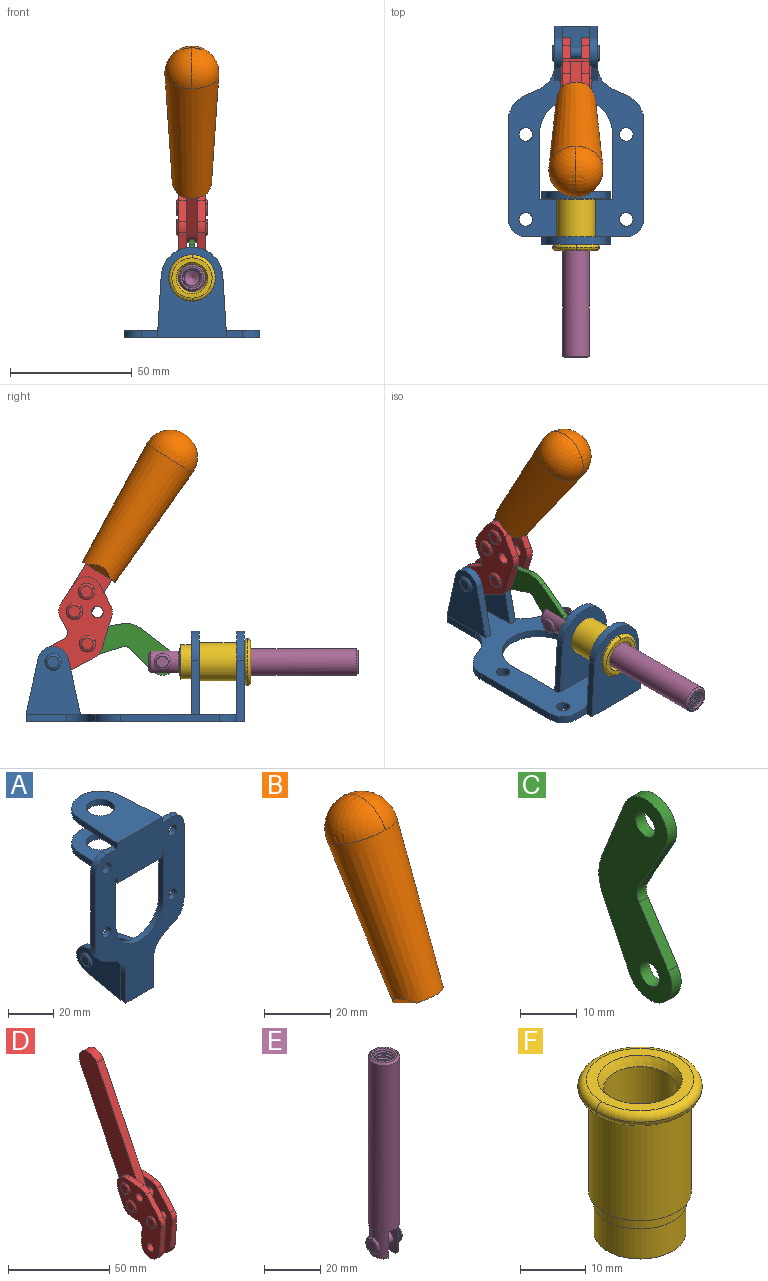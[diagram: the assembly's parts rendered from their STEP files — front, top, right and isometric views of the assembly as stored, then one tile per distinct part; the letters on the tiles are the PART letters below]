
ASSEMBLY  parts=6 mates=6
PART A: 55 faces, bbox 55.7x37.4x89.8 mm
  f0: torus R=2.41mm, axis (-1,0,0), area 15mm2, adj f11,f15,f25
  f1: torus R=2.41mm, axis (-1,0,0), area 15mm2, adj f10,f12,f22
  f2: cylinder r=2.78mm len=5.56mm, axis (0,-1,0), area 54.2mm2, adj f30,f54
  f3: cylinder r=14.99mm len=29.97mm, axis (0,-1,0), area 145.9mm2, adj f30,f49,f53,f54
  f4: cylinder r=2.78mm len=5.56mm, axis (0,-1,0), area 54.2mm2, adj f30,f54
  f5: cylinder r=2.78mm len=5.56mm, axis (0,-1,0), area 54.2mm2, adj f30,f54
  f6: cylinder r=2.78mm len=5.56mm, axis (0,-1,0), area 54.2mm2, adj f30,f54
  f7: cylinder r=6.35mm len=12.7mm, axis (0,0,1), area 123.6mm2, adj f27,f51
  f8: cylinder r=6.35mm len=12.7mm, axis (0,0,-1), area 124.7mm2, adj f21,f35
  f9: cylinder r=2.41mm len=11.18mm, axis (-1,0,0), area 169.4mm2, adj f16,f19
  f10: plane 4.83x4.83mm, normal (1,0,0), area 18.3mm2, adj f1,f12
  f11: plane 4.83x4.83mm, normal (-1,0,0), area 18.3mm2, adj f0,f15
  f12: torus R=2.41mm, axis (-1,0,0), area 15mm2, adj f1,f10,f22
  f13: cylinder r=6.35mm len=12.41mm, axis (1,0,0), area 53.4mm2, adj f18,f19,f22,f23
  f14: cylinder r=6.35mm len=12.41mm, axis (-1,0,0), area 53.4mm2, adj f16,f17,f24,f25
  f15: torus R=2.41mm, axis (-1,0,0), area 15mm2, adj f0,f11,f25
  f16: plane 27.86x22.35mm, normal (1,0,0), area 425.4mm2, adj f9,f14,f17,f24,f30
  f17: plane 22.86x4.97mm, normal (0,0.21,0.98), area 72.5mm2, adj f14,f16,f25,f30
  f18: plane 22.86x4.97mm, normal (0,0.21,0.98), area 72.5mm2, adj f13,f19,f22,f30
  f19: plane 27.86x22.35mm, normal (-1,0,0), area 425.4mm2, adj f9,f13,f18,f23,f30
  f20: cylinder r=12.7mm len=25.35mm, axis (0,0,-1), area 119.8mm2, adj f21,f34,f35,f36
  f21: plane 34.21x28.07mm, normal (0,0,-1), area 702.4mm2, adj f8,f20,f30,f34,f36
  f22: plane 27.96x22.45mm, normal (1,0,0), area 407.2mm2, adj f1,f12,f13,f18,f23,f30,f42,f43
  f23: plane 22.86x4.97mm, normal (0,0.21,-0.98), area 72.5mm2, adj f13,f19,f22,f44
  f24: plane 22.86x4.97mm, normal (0,0.21,-0.98), area 72.5mm2, adj f14,f16,f25,f44
  f25: plane 27.86x22.35mm, normal (-1,0,0), area 407.1mm2, adj f0,f14,f15,f17,f24,f30,f45,f46
  f26: plane 3.1x0.95mm, normal (0,0,-1), area 2.7mm2, adj f30,f49,f50,f54
  f27: plane 34.21x28.07mm, normal (0,0,1), area 702.4mm2, adj f7,f28,f30,f50,f52
  f28: cylinder r=12.7mm len=25.35mm, axis (0,0,1), area 118.8mm2, adj f27,f50,f51,f52
  f29: plane 3.1x0.95mm, normal (0,0,-1), area 2.7mm2, adj f30,f52,f53,f54
  f30: plane 86.54x55.63mm, normal (0,1,0), area 2362.9mm2, adj f2,f3,f4,f5,f6,f16,f17,f18
  f31: plane 40.56x3.1mm, normal (-1,0,0), area 125.7mm2, adj f30,f32,f48,f54
  f32: cylinder r=7.11mm len=7.11mm, axis (0,-1,0), area 34.6mm2, adj f30,f31,f33,f54
  f33: plane 6.67x3.1mm, normal (0,0,1), area 20.4mm2, adj f30,f32,f34,f54
  f34: plane 25.39x3.13mm, normal (-1,0.06,0), area 79.5mm2, adj f20,f21,f33,f35,f54
  f35: plane 37.31x28.45mm, normal (0,0,1), area 789.9mm2, adj f8,f20,f34,f36,f54
  f36: plane 25.39x3.13mm, normal (1,0.06,0), area 79.5mm2, adj f20,f21,f35,f37,f54
  f37: plane 6.67x3.1mm, normal (0,0,1), area 20.4mm2, adj f30,f36,f38,f54
  f38: cylinder r=7.11mm len=7.11mm, axis (0,-1,0), area 34.6mm2, adj f30,f37,f39,f54
  f39: plane 40.56x3.1mm, normal (1,0,0), area 125.7mm2, adj f30,f38,f40,f54
  f40: cylinder r=11.18mm len=10.16mm, axis (0,-1,0), area 39.5mm2, adj f30,f39,f41,f54
  f41: plane 6.09x3.1mm, normal (0.42,0,-0.91), area 20.8mm2, adj f30,f40,f42,f54
  f42: cylinder r=11.18mm len=9.41mm, axis (0,-1,0), area 37.2mm2, adj f22,f30,f41,f43,f54
  f43: plane 16.5x3.1mm, normal (1,0,0), area 51.1mm2, adj f22,f42,f44,f54
  f44: plane 17.37x3.1mm, normal (0,0,-1), area 53.8mm2, adj f23,f24,f30,f43,f45,f54
  f45: plane 16.5x3.1mm, normal (-1,0,0), area 51.1mm2, adj f25,f44,f46,f54
  f46: cylinder r=11.18mm len=9.41mm, axis (0,-1,0), area 37.2mm2, adj f25,f30,f45,f47,f54
  f47: plane 6.09x3.1mm, normal (-0.42,0,-0.91), area 20.8mm2, adj f30,f46,f48,f54
  f48: cylinder r=11.18mm len=10.16mm, axis (0,-1,0), area 39.5mm2, adj f30,f31,f47,f54
  f49: plane 26.54x3.1mm, normal (-1,0,0), area 82.3mm2, adj f3,f26,f30,f54
  f50: plane 25.39x3.1mm, normal (1,0.06,0), area 78.8mm2, adj f26,f27,f28,f51,f54
  f51: plane 37.31x28.45mm, normal (0,0,-1), area 789.9mm2, adj f7,f28,f50,f52,f54
  f52: plane 25.39x3.1mm, normal (-1,0.06,0), area 78.8mm2, adj f27,f28,f29,f51,f54
  f53: plane 26.54x3.1mm, normal (1,0,0), area 82.3mm2, adj f3,f29,f30,f54
  f54: plane 89.66x55.63mm, normal (0,-1,0), area 2678.5mm2, adj f2,f3,f4,f5,f6,f26,f29,f31
PART B: 11 faces, bbox 22.3x42.6x64.5 mm
  f0: sphere r=11.13mm, area 411.4mm2, adj f1,f8
  f1: cone r=11.11mm half-angle=3.3deg, axis (0,0.44,0.9), area 3251.8mm2, adj f0,f7,f8,f9,f10
  f2: cylinder r=6.16mm len=11.7mm, axis (1,0,0), area 89.5mm2, adj f3,f4,f5,f6
  f3: plane 60.23x36.75mm, normal (-1,0,0), area 763.6mm2, adj f2,f4,f6,f10
  f4: plane 51.37x25.05mm, normal (0,0.9,-0.44), area 264.2mm2, adj f2,f3,f5,f10
  f5: plane 60.23x36.75mm, normal (1,0,0), area 763.6mm2, adj f2,f4,f6,f10
  f6: plane 51.37x25.05mm, normal (0,-0.9,0.44), area 264.2mm2, adj f2,f3,f5,f10
  f7: plane 9.95x5.95mm, normal (0.71,-0.31,-0.64), area 25.8mm2, adj f1,f10
  f8: sphere r=11.13mm, area 411.4mm2, adj f0,f1
  f9: plane 9.95x5.95mm, normal (-0.71,-0.31,-0.64), area 25.8mm2, adj f1,f10
  f10: plane 14.27x11.38mm, normal (0,-0.44,-0.9), area 106.7mm2, adj f1,f3,f4,f5,f6,f7,f9
PART C: 12 faces, bbox 2.3x18.2x42.8 mm
  f0: cylinder r=2.4mm len=4.8mm, axis (1,0,0), area 34.9mm2, adj f4,f11
  f1: cylinder r=10.41mm len=8.47mm, axis (1,0,0), area 20.2mm2, adj f4,f9,f10,f11
  f2: cylinder r=3.05mm len=3.16mm, axis (1,0,0), area 7.7mm2, adj f4,f6,f7,f11
  f3: cylinder r=2.4mm len=4.8mm, axis (1,0,0), area 34.9mm2, adj f4,f11
  f4: plane 42.81x18.23mm, normal (-1,0,0), area 414.1mm2, adj f0,f1,f2,f3,f5,f6,f7,f8
  f5: cylinder r=5.54mm len=10.67mm, axis (1,0,0), area 41.8mm2, adj f4,f6,f10,f11
  f6: plane 11.66x6.53mm, normal (0,-0.87,-0.49), area 30.9mm2, adj f2,f4,f5,f11
  f7: plane 11.17x7.33mm, normal (0,-0.84,0.55), area 30.9mm2, adj f2,f4,f8,f11
  f8: cylinder r=5.54mm len=10.51mm, axis (1,0,0), area 41.8mm2, adj f4,f7,f9,f11
  f9: plane 13.67x6.67mm, normal (0,0.9,-0.44), area 35.1mm2, adj f1,f4,f8,f11
  f10: plane 14.1x5.7mm, normal (0,0.93,0.37), area 35.1mm2, adj f1,f4,f5,f11
  f11: plane 42.81x18.23mm, normal (1,0,0), area 414.1mm2, adj f0,f1,f2,f3,f5,f6,f7,f8
PART D: 59 faces, bbox 12.9x60.2x99.6 mm
  f0: torus R=2.39mm, axis (-1,0,0), area 14.9mm2, adj f20,f43,f51
  f1: torus R=2.39mm, axis (-1,0,0), area 14.9mm2, adj f19,f42,f51
  f2: torus R=2.39mm, axis (-1,0,0), area 14.9mm2, adj f18,f35,f51
  f3: torus R=2.39mm, axis (-1,0,0), area 14.9mm2, adj f14,f17,f23
  f4: torus R=2.39mm, axis (-1,0,0), area 14.9mm2, adj f13,f16,f23
  f5: torus R=2.39mm, axis (-1,0,0), area 14.9mm2, adj f12,f15,f23
  f6: cylinder r=2.39mm len=4.78mm, axis (1,0,0), area 46.5mm2, adj f48,f50,f51
  f7: cylinder r=2.39mm len=4.78mm, axis (1,0,0), area 46.5mm2, adj f50,f51
  f8: cylinder r=6.35mm len=12.68mm, axis (1,0,0), area 61.8mm2, adj f38,f39,f50,f51
  f9: cylinder r=2.39mm len=4.78mm, axis (-1,0,0), area 70.5mm2, adj f46,f50
  f10: cylinder r=2.39mm len=4.78mm, axis (-1,0,0), area 46.5mm2, adj f23,f45,f46
  f11: cylinder r=2.39mm len=4.78mm, axis (-1,0,0), area 46.5mm2, adj f23,f46
  f12: plane 4.78x4.78mm, normal (1,0,0), area 17.9mm2, adj f5,f15
  f13: plane 4.78x4.78mm, normal (1,0,0), area 17.9mm2, adj f4,f16
  f14: plane 4.78x4.78mm, normal (1,0,0), area 17.9mm2, adj f3,f17
  f15: torus R=2.39mm, axis (-1,0,0), area 14.9mm2, adj f5,f12,f23
  f16: torus R=2.39mm, axis (-1,0,0), area 14.9mm2, adj f4,f13,f23
  f17: torus R=2.39mm, axis (-1,0,0), area 14.9mm2, adj f3,f14,f23
  f18: plane 4.78x4.78mm, normal (-1,0,0), area 17.9mm2, adj f2,f35
  f19: plane 4.78x4.78mm, normal (-1,0,0), area 17.9mm2, adj f1,f42
  f20: plane 4.78x4.78mm, normal (-1,0,0), area 17.9mm2, adj f0,f43
  f21: plane 2.26x0.2mm, normal (1,0,0), area 0.2mm2, adj f31,f44
  f22: plane 2.26x0.2mm, normal (-1,0,0), area 0.2mm2, adj f41,f44
  f23: plane 39.37x30.77mm, normal (1,0,0), area 565.5mm2, adj f3,f4,f5,f10,f11,f15,f16,f17
  f24: cylinder r=6.1mm len=4.15mm, axis (-1,0,0), area 14.7mm2, adj f23,f25,f32,f46
  f25: plane 10.25x9.01mm, normal (0,-0.75,0.66), area 42.3mm2, adj f23,f24,f26,f46
  f26: cylinder r=6.35mm len=4.64mm, axis (-1,0,0), area 15.6mm2, adj f23,f25,f27,f46
  f27: plane 15.84x3.1mm, normal (0,-1,-0.07), area 49.2mm2, adj f23,f26,f28,f46
  f28: cylinder r=6.35mm len=12.68mm, axis (-1,0,0), area 61.8mm2, adj f23,f27,f29,f46
  f29: plane 8.11x3.1mm, normal (0,1,0.07), area 25.2mm2, adj f23,f28,f30,f46
  f30: cylinder r=3.05mm len=3.25mm, axis (-1,0,0), area 14.8mm2, adj f23,f29,f31,f46
  f31: plane 5.99x3.1mm, normal (0,0.07,-1), area 18.6mm2, adj f21,f23,f30,f44,f46
  f32: plane 9.5x3.1mm, normal (0,-0.07,1), area 29.5mm2, adj f23,f24,f33,f46,f47
  f33: cylinder r=6.1mm len=8.63mm, axis (-1,0,0), area 39.1mm2, adj f23,f32,f34,f47
  f34: plane 8.65x3.96mm, normal (0,0.91,-0.42), area 29.5mm2, adj f23,f33,f44,f47
  f35: torus R=2.39mm, axis (-1,0,0), area 14.9mm2, adj f2,f18,f51
  f36: plane 10.25x9.01mm, normal (0,-0.75,0.66), area 42.3mm2, adj f37,f49,f50,f51
  f37: cylinder r=6.35mm len=4.64mm, axis (1,0,0), area 15.6mm2, adj f36,f38,f50,f51
  f38: plane 15.84x3.1mm, normal (0,-1,-0.07), area 49.2mm2, adj f8,f37,f50,f51
  f39: plane 8.11x3.1mm, normal (0,1,0.07), area 25.2mm2, adj f8,f40,f50,f51
  f40: cylinder r=3.05mm len=3.25mm, axis (1,0,0), area 14.8mm2, adj f39,f41,f50,f51
  f41: plane 5.99x3.1mm, normal (0,0.07,-1), area 18.6mm2, adj f22,f40,f44,f50,f51
  f42: torus R=2.39mm, axis (-1,0,0), area 14.9mm2, adj f1,f19,f51
  f43: torus R=2.39mm, axis (-1,0,0), area 14.9mm2, adj f0,f20,f51
  f44: cylinder r=6.35mm len=12.12mm, axis (-1,0,0), area 128.9mm2, adj f21,f22,f23,f31,f34,f41,f46,f47
  f45: plane 2.65x1.35mm, normal (1,0,0), area 1mm2, adj f10,f55
  f46: plane 39.08x20.42mm, normal (-1,0,0), area 412.5mm2, adj f9,f10,f11,f24,f25,f26,f27,f28
  f47: plane 77.62x39.82mm, normal (1,0,0), area 850mm2, adj f32,f33,f34,f44,f53,f54,f55
  f48: plane 2.65x1.35mm, normal (-1,0,0), area 1mm2, adj f6,f55
  f49: cylinder r=6.1mm len=4.15mm, axis (1,0,0), area 14.7mm2, adj f36,f50,f51,f56
  f50: plane 39.08x20.42mm, normal (1,0,0), area 412.5mm2, adj f6,f7,f8,f9,f36,f37,f38,f39
  f51: plane 39.37x30.77mm, normal (-1,0,0), area 565.5mm2, adj f0,f1,f2,f6,f7,f8,f35,f36
  f52: plane 8.65x3.96mm, normal (0,0.91,-0.42), area 29.5mm2, adj f44,f51,f57,f58
  f53: plane 68.49x33.4mm, normal (0,0.9,-0.44), area 358.1mm2, adj f44,f47,f54,f58
  f54: cylinder r=6.35mm len=12.06mm, axis (1,0,0), area 93.7mm2, adj f47,f53,f55,f58
  f55: plane 68.49x33.4mm, normal (0,-0.9,0.44), area 358.1mm2, adj f44,f45,f46,f47,f48,f50,f54,f58
  f56: plane 9.5x3.1mm, normal (0,-0.07,1), area 29.5mm2, adj f49,f50,f51,f57,f58
  f57: cylinder r=6.1mm len=8.63mm, axis (1,0,0), area 39.1mm2, adj f51,f52,f56,f58
  f58: plane 77.62x39.82mm, normal (-1,0,0), area 850mm2, adj f44,f52,f53,f54,f55,f56,f57
PART E: 48 faces, bbox 12.6x11.1x86.1 mm
  f0: torus R=2.41mm, axis (-1,0,0), area 15mm2, adj f30,f32,f34
  f1: torus R=2.41mm, axis (-1,0,0), area 15mm2, adj f29,f31,f33
  f2: cylinder r=5.54mm len=72.39mm, axis (0,0,1), area 2518.5mm2, adj f3,f4,f42,f43
  f3: cone r=5.54mm half-angle=45deg, axis (0,0,1), area 7.6mm2, adj f2,f5,f41
  f4: cone r=5.54mm half-angle=45deg, axis (0,0,-1), area 34.9mm2, adj f2,f39
  f5: cylinder r=5.08mm len=11.48mm, axis (0,0,1), area 108.3mm2, adj f3,f7,f8,f41
  f6: cylinder r=2.41mm len=4.83mm, axis (-1,0,0), area 71.2mm2, adj f40,f41
  f7: cylinder r=2.41mm len=4.83mm, axis (-1,0,0), area 7.6mm2, adj f5,f34
  f8: cone r=5.08mm half-angle=45deg, axis (0,0,1), area 10.6mm2, adj f5,f37,f41
  f9: cone r=3.98mm half-angle=45deg, axis (0,0,1), area 17.6mm2, adj f27,f39,f45,f46,f47
  f10: cylinder r=2.41mm len=4.83mm, axis (-1,0,0), area 7.6mm2, adj f33,f38
  f11: cylinder r=3.2mm len=6.4mm, axis (0,0,1), area 78.4mm2, adj f12,f28,f44,f45,f47
  f12: cylinder r=3.2mm len=6.4mm, axis (0,0,1), area 10.5mm2, adj f11,f13,f45,f47
  f13: cylinder r=3.2mm len=6.4mm, axis (0,0,1), area 10.5mm2, adj f12,f14,f45,f47
  f14: cylinder r=3.2mm len=6.4mm, axis (0,0,1), area 10.5mm2, adj f13,f15,f45,f47
  f15: cylinder r=3.2mm len=6.4mm, axis (0,0,1), area 10.5mm2, adj f14,f16,f45,f47
  f16: cylinder r=3.2mm len=6.4mm, axis (0,0,1), area 10.5mm2, adj f15,f17,f45,f47
  f17: cylinder r=3.2mm len=6.4mm, axis (0,0,1), area 10.5mm2, adj f16,f18,f45,f47
  f18: cylinder r=3.2mm len=6.4mm, axis (0,0,1), area 10.5mm2, adj f17,f19,f45,f47
  f19: cylinder r=3.2mm len=6.4mm, axis (0,0,1), area 10.5mm2, adj f18,f20,f45,f47
  f20: cylinder r=3.2mm len=6.4mm, axis (0,0,1), area 10.5mm2, adj f19,f21,f45,f47
  f21: cylinder r=3.2mm len=6.4mm, axis (0,0,1), area 10.5mm2, adj f20,f22,f45,f47
  f22: cylinder r=3.2mm len=6.4mm, axis (0,0,1), area 10.5mm2, adj f21,f23,f45,f47
  f23: cylinder r=3.2mm len=6.4mm, axis (0,0,1), area 10.5mm2, adj f22,f24,f45,f47
  f24: cylinder r=3.2mm len=6.4mm, axis (0,0,1), area 10.5mm2, adj f23,f25,f45,f47
  f25: cylinder r=3.2mm len=6.4mm, axis (0,0,1), area 10.5mm2, adj f24,f26,f45,f47
  f26: cylinder r=3.2mm len=6.4mm, axis (0,0,1), area 10.5mm2, adj f25,f27,f45,f47
  f27: cylinder r=3.2mm len=6.4mm, axis (0,0,1), area 7.4mm2, adj f9,f26,f45,f47
  f28: cone r=3.2mm half-angle=60deg, axis (0,0,1), area 37.2mm2, adj f11
  f29: plane 4.83x4.83mm, normal (-1,0,0), area 18.3mm2, adj f1,f31
  f30: plane 4.83x4.83mm, normal (1,0,0), area 18.3mm2, adj f0,f32
  f31: torus R=2.41mm, axis (-1,0,0), area 15mm2, adj f1,f29,f33
  f32: torus R=2.41mm, axis (-1,0,0), area 15mm2, adj f0,f30,f34
  f33: plane 6.83x6.83mm, normal (1,0,0), area 18.3mm2, adj f1,f10,f31
  f34: plane 6.83x6.83mm, normal (-1,0,0), area 18.3mm2, adj f0,f7,f32
  f35: cone r=5.08mm half-angle=45deg, axis (0,0,1), area 10.6mm2, adj f36,f38,f40
  f36: plane 7.25x1.97mm, normal (0,0,-1), area 10mm2, adj f35,f40
  f37: plane 7.25x1.97mm, normal (0,0,-1), area 10mm2, adj f8,f41
  f38: cylinder r=5.08mm len=11.48mm, axis (0,0,1), area 108.3mm2, adj f10,f35,f40,f42
  f39: plane 9.55x9.55mm, normal (0,0,1), area 22mm2, adj f4,f9
  f40: plane 12.76x10.09mm, normal (1,0,0), area 95.7mm2, adj f6,f35,f36,f38,f42,f43
  f41: plane 12.76x10.09mm, normal (-1,0,0), area 95.7mm2, adj f3,f5,f6,f8,f37,f43
  f42: cone r=5.54mm half-angle=45deg, axis (0,0,1), area 7.6mm2, adj f2,f38,f40
  f43: plane 11.07x4.7mm, normal (0,0,-1), area 50.4mm2, adj f2,f40,f41
  f44: plane 0.89x0.62mm, normal (-1,0,0), area 0.3mm2, adj f11,f45,f46,f47
  f45: bspline ~24.8x7.63mm, area 266.6mm2, adj f9,f11,f12,f13,f14,f15,f16,f17
  f46: bspline ~24.87x7.63mm, area 73.6mm2, adj f9,f44,f45,f47
  f47: bspline ~24.98x7.63mm, area 272.5mm2, adj f9,f11,f12,f13,f14,f15,f16,f17
PART F: 15 faces, bbox 20.6x20.6x28.7 mm
  f0: torus R=8.26mm, axis (0,0,1), area 56.8mm2, adj f1,f10,f12
  f1: torus R=8.26mm, axis (0,0,1), area 56.8mm2, adj f0,f6,f13
  f2: cylinder r=5.59mm len=25.91mm, axis (0,0,1), area 909.6mm2, adj f3,f4
  f3: cone r=6.86mm half-angle=45deg, axis (0,0,-1), area 70.2mm2, adj f2,f14
  f4: cone r=6.47mm half-angle=30deg, axis (0,0,1), area 66.7mm2, adj f2,f13
  f5: cylinder r=7.04mm len=14.07mm, axis (0,0,1), area 252.6mm2, adj f11,f14
  f6: torus R=8.26mm, axis (0,0,1), area 56.8mm2, adj f1,f12,f13
  f7: cylinder r=7.16mm len=14.33mm, axis (0,0,1), area 91.5mm2, adj f9,f11
  f8: cylinder r=7.86mm len=18.42mm, axis (0,0,1), area 909.6mm2, adj f9,f10
  f9: plane 15.72x15.72mm, normal (0,0,-1), area 33mm2, adj f7,f8
  f10: plane 16.51x16.51mm, normal (0,0,-1), area 19.9mm2, adj f0,f8,f12
  f11: plane 14.33x14.33mm, normal (0,0,-1), area 5.7mm2, adj f5,f7
  f12: torus R=8.26mm, axis (0,0,1), area 56.8mm2, adj f0,f6,f10
  f13: plane 16.51x16.51mm, normal (0,0,1), area 82.7mm2, adj f1,f4,f6
  f14: plane 14.07x14.07mm, normal (0,0,-1), area 7.8mm2, adj f3,f5
PLACE A rot(axis=(1,0,0),90deg) t=(0,1.23,0)mm fixed
PLACE B rot(axis=(1,0,0),57.9deg) t=(-0.04,-6.94,20.8)mm
PLACE C rot(axis=(1,0,0),105.6deg) t=(0,9.98,5.07)mm
PLACE D rot(axis=(1,0,0),57.9deg) t=(0,-6.94,20.8)mm
PLACE E rot(axis=(1,0,0),90deg) t=(0,3.93,0)mm
PLACE F rot(axis=(0.58,-0.58,0.58),120deg) t=(24.61,1.23,24.61)mm
MATE slider A.f7 <-> E.f2  axis (0,-1,0) through (0,-45.16,24.61)mm
MATE revolute E.f6 <-> C.f5  axis (-1,0,0) through (0,-11.54,24.61)mm
MATE revolute C.f3 <-> D.f4  axis (1,0,0) through (0,19.32,32.08)mm
MATE revolute D.f7 <-> A.f0  axis (1,0,0) through (0,33.32,24.61)mm
MATE fastened B.f2 <-> D.f54  axis (1,0,0) through (-2.35,-15.63,110.08)mm
MATE fastened F.f2 <-> A.f7  axis (0,1,0) through (0,-45.16,24.61)mm
